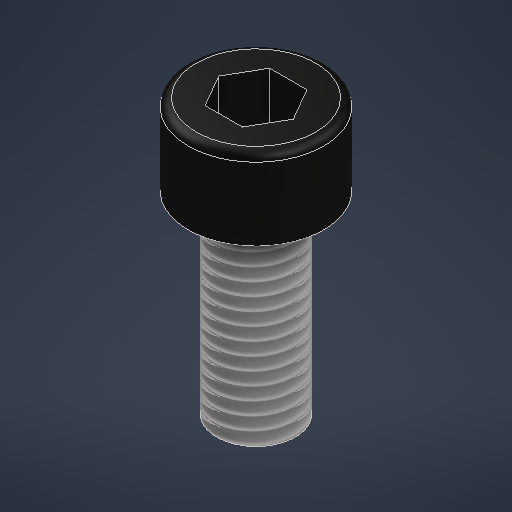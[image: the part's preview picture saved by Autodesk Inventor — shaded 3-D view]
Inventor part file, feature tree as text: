
AUTODESK INVENTOR PART (.ipt)
format: ipt  version: 2025.1 (Build 291241000, 241)  size: 269,312 bytes
history: native  units: mm
features: extrude x3, sketch x1, fillet x1, thread x1
ambient origin geometry x8: Origin, YZ Plane, XZ Plane, XY Plane, X Axis, Y Axis, Z Axis, Center Point
bodies: Solid1 (feature_tree)
feature tree (6):
  sketch  "Sketch1"  dims[d0=4.88mm d1=8.4mm d2=5.0mm d3=0.0mm d4=12.0mm d5=0.0mm d8=4.0mm d9=3.0mm d10=0.0mm d11=0.5mm d12=20.0mm d13=0.0mm]
  extrude  "Extrusion1"  Depth=0.5mm
  extrude  "Extrusion2"  Depth=5.0mm TaperAngle=0.0deg
  extrude  "Extrusion3"  Depth=12.0mm
  fillet  "Fillet1"  [1 undecoded]
  thread  "Thread2"  [1 undecoded]
note: 2 required parameter values undecoded (feature->parameter linkage not recoverable at this tier; creation-order binding heuristic only, values carry confidence <= 0.55)
